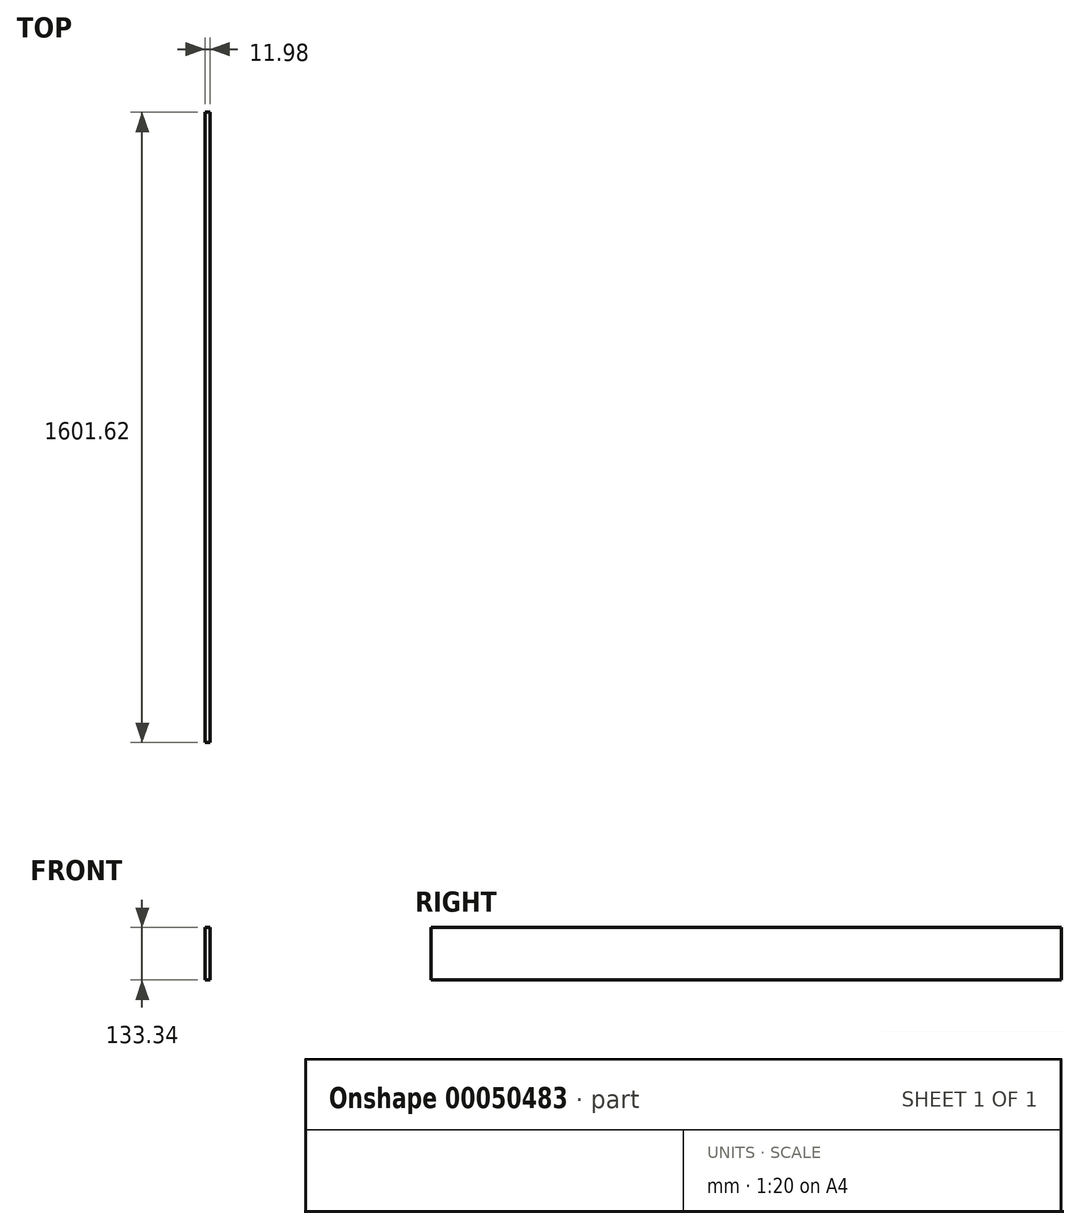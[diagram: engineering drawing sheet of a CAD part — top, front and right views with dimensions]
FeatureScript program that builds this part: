
annotation { "Feature Type Name" : "Feature", "Feature Type Description" : "" }
export const myFeature = defineFeature(function(context is Context, id is Id, definition is map)
    precondition{}
    {
        {
            var Q0;
            Q0=qCreatedBy(makeId("Right.planeOp"),FACE);
            var sketch = newSketch(context, id + "F0", { "sketchPlane" : qUnion([Q0])});
            skLineSegment(sketch, "E0.rect.bottom", {"start": v(800.81, -66.67) * mm, "end": v(-800.81, -66.67) * mm});
            skLineSegment(sketch, "E0.rect.top", {"start": v(800.81, 66.68) * mm, "end": v(-800.81, 66.67) * mm});
            skLineSegment(sketch, "E0.rect.left", {"start": v(800.81, -66.67) * mm, "end": v(800.81, 66.68) * mm});
            skLineSegment(sketch, "E0.rect.right", {"start": v(-800.81, -66.67) * mm, "end": v(-800.81, 66.68) * mm});
            skPoint(sketch, "E0.rect.middle", {"position": v(0, 0) * mm});
            skSolve(sketch);
        }
        {
            var Q0;
            Q0 = qSketchRegion(id + "F0", true);
            extrude(context, id + "F1", {"entities" : qUnion([Q0]), "endBound" : BoundingType.SYMMETRIC, "depth" : 12 * mm});
        }
    });
